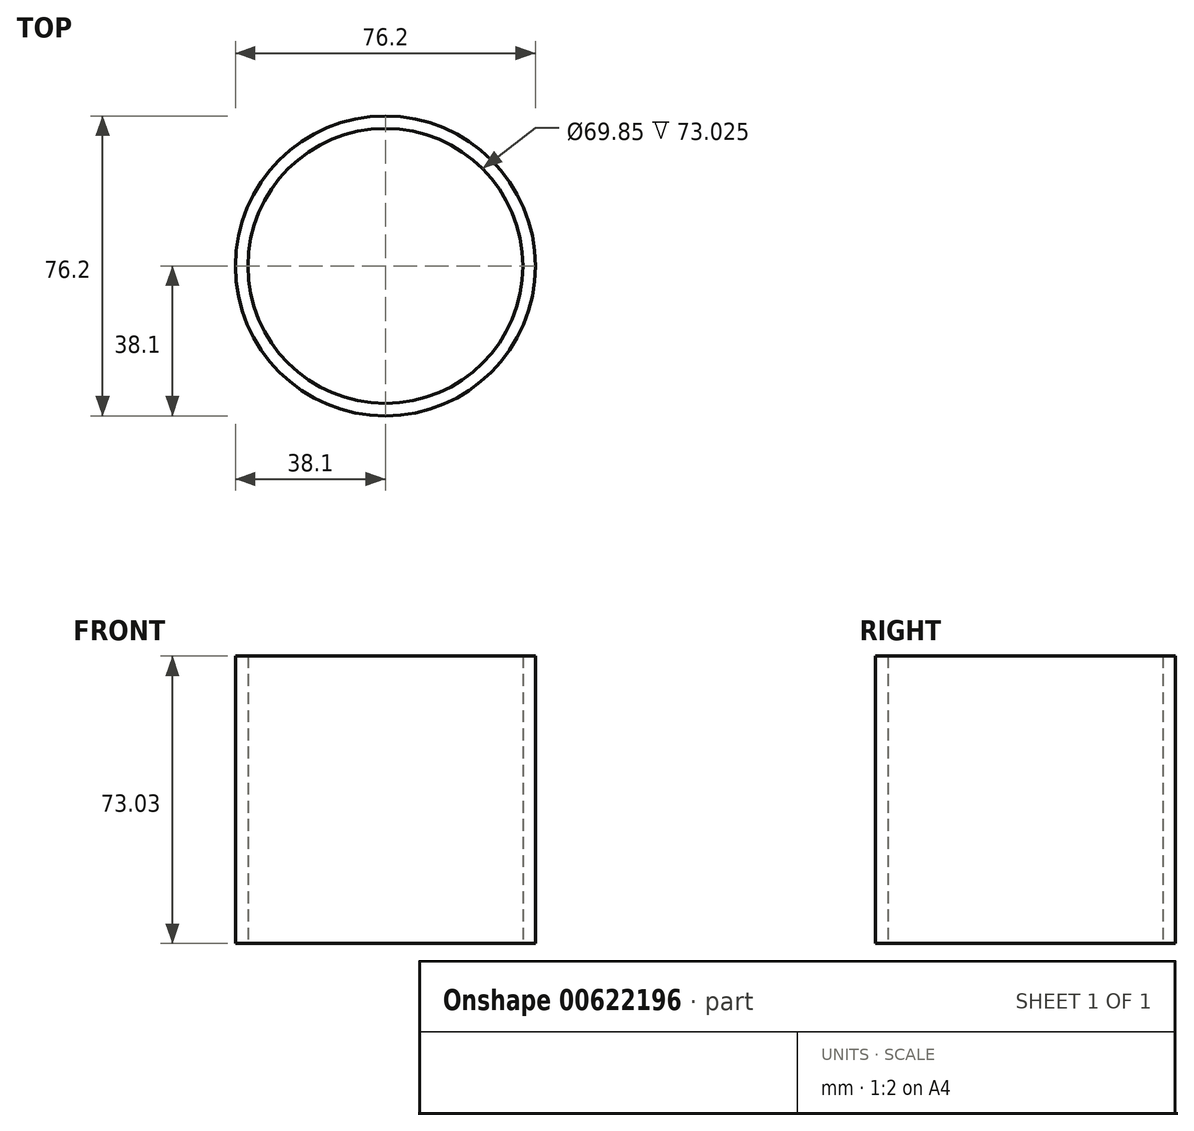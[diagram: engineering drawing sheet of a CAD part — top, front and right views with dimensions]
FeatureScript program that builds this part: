
annotation { "Feature Type Name" : "Feature", "Feature Type Description" : "" }
export const myFeature = defineFeature(function(context is Context, id is Id, definition is map)
    precondition{}
    {
        {
            var Q0;
            Q0=qCreatedBy(makeId("Top.planeOp"),FACE);
            var sketch = newSketch(context, id + "F0", { "sketchPlane" : qUnion([Q0])});
            skCircle(sketch, "E0", {"center": v(0, 0) * mm, "radius": 38.1 * mm});
            skCircle(sketch, "E1", {"center": v(0, 0) * mm, "radius": 34.93 * mm});
            skSolve(sketch);
        }
        {
            var Q0;
            Q0 = qSketchRegion(id + "F0", true);
            extrude(context, id + "F1", {"entities" : qUnion([Q0]), "depth" : 73.02 * mm, "offsetDistance" : 25.4 * mm});
        }
    });
